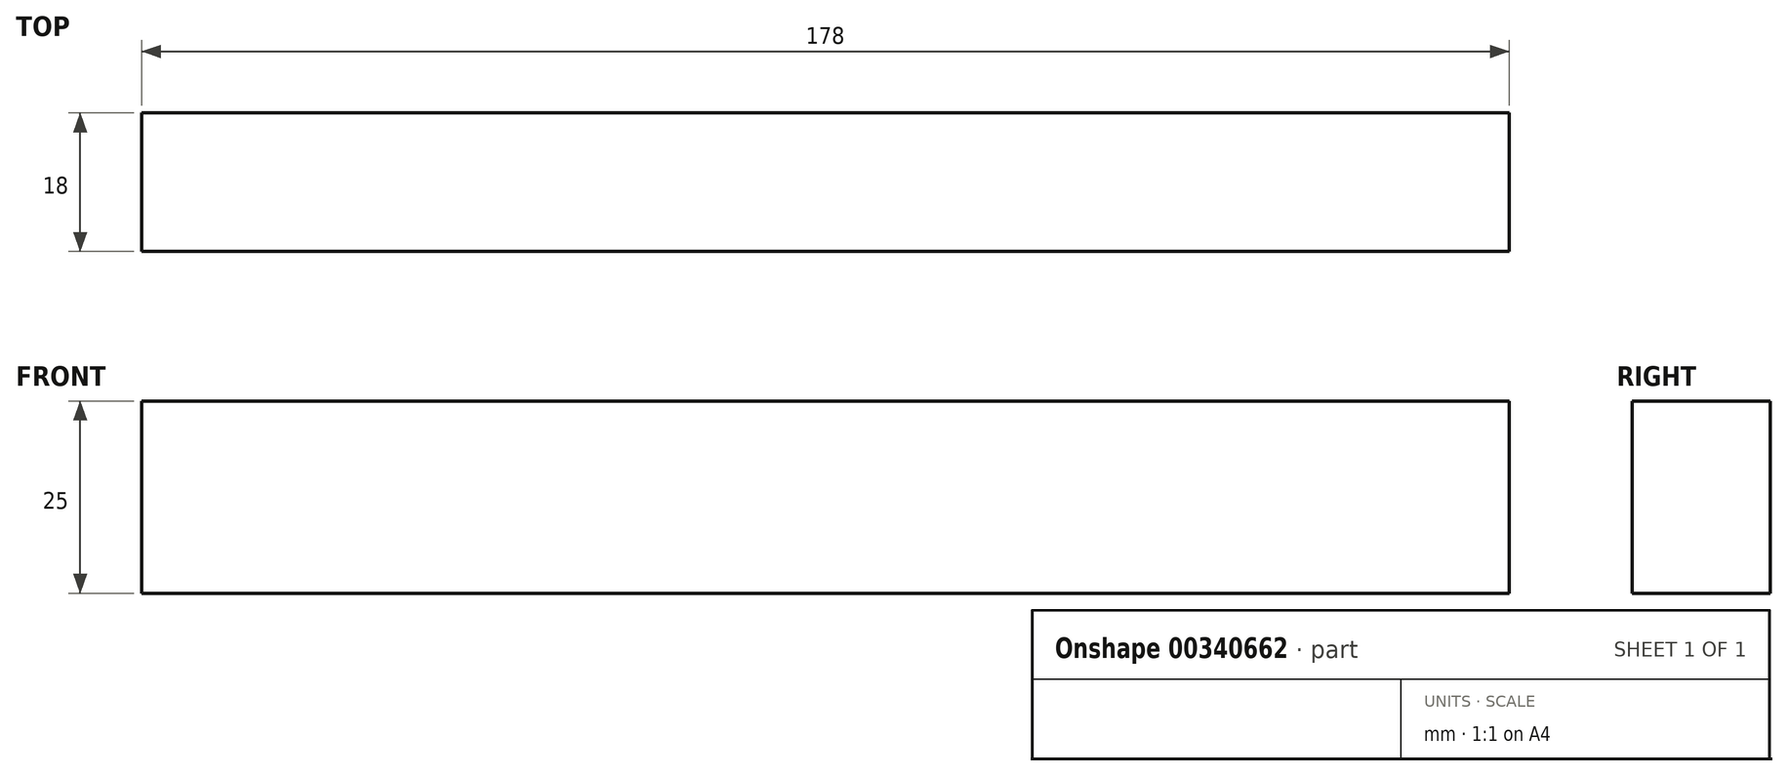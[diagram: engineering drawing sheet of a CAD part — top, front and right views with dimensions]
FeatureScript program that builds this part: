
annotation { "Feature Type Name" : "Feature", "Feature Type Description" : "" }
export const myFeature = defineFeature(function(context is Context, id is Id, definition is map)
    precondition{}
    {
        {
            var Q0;
            Q0=qCreatedBy(makeId("Front.planeOp"),FACE);
            var sketch = newSketch(context, id + "F0", { "sketchPlane" : qUnion([Q0])});
            skLineSegment(sketch, "E0.bottom", {"start": v(-84.61, -5.31) * mm, "end": v(93.39, -5.31) * mm});
            skLineSegment(sketch, "E0.top", {"start": v(-84.61, -30.31) * mm, "end": v(93.39, -30.31) * mm});
            skLineSegment(sketch, "E0.left", {"start": v(-84.61, -5.31) * mm, "end": v(-84.61, -30.31) * mm});
            skLineSegment(sketch, "E0.right", {"start": v(93.39, -5.31) * mm, "end": v(93.39, -30.31) * mm});
            skSolve(sketch);
        }
        {
            var Q0;
            Q0=makeQuery(id+"F0.imprint","IMPRINT",FACE,{"disambiguationData":[TD([[makeQuery(id+"F0.imprint","IMPRINT",EDGE,{"derivedFrom":sQuery(id+"F0.wireOp",EDGE,"E0.bottom")}),-1.0]])]});
            extrude(context, id + "F1", {"entities" : qUnion([Q0]), "depth" : 18 * mm});
        }
    });
